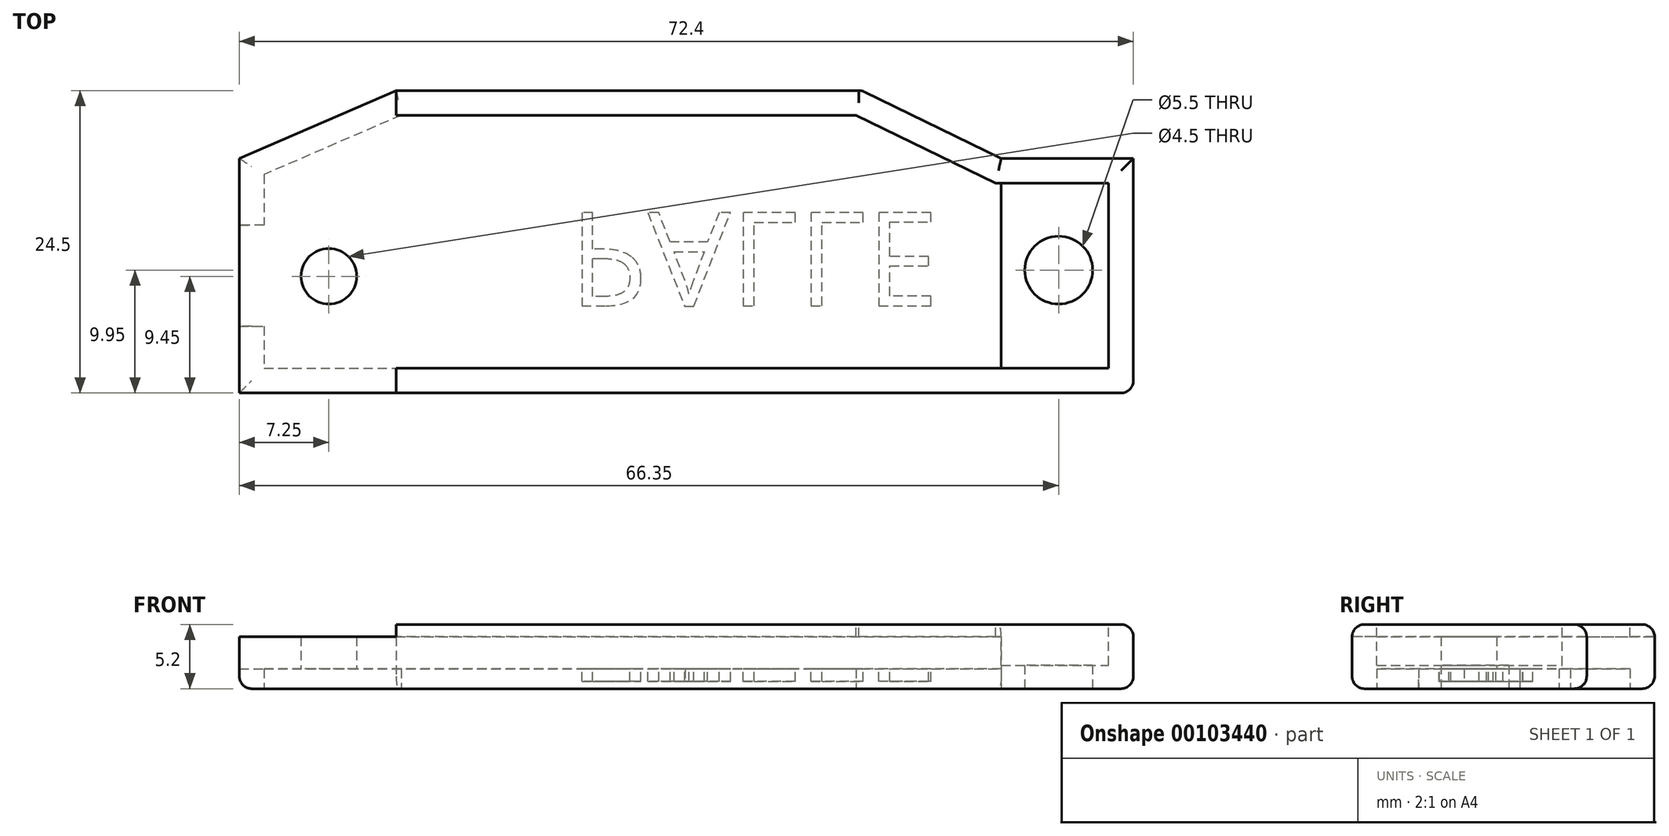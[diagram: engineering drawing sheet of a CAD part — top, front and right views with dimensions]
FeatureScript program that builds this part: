
annotation { "Feature Type Name" : "Feature", "Feature Type Description" : "" }
export const myFeature = defineFeature(function(context is Context, id is Id, definition is map)
    precondition{}
    {
        {
            var Q0;
            Q0=qCreatedBy(makeId("Top.planeOp"),FACE);
            var sketch = newSketch(context, id + "F0", { "sketchPlane" : qUnion([Q0])});
            skLineSegment(sketch, "E0.bottom", {"start": v(-23.5, 12.25) * mm, "end": v(14.2, 12.25) * mm});
            skLineSegment(sketch, "E0.top", {"start": v(-36.2, -12.25) * mm, "end": v(36.2, -12.25) * mm});
            skLineSegment(sketch, "E0.left", {"start": v(-36.2, 6.75) * mm, "end": v(-36.2, -12.25) * mm});
            skLineSegment(sketch, "E0.right", {"start": v(36.2, 6.75) * mm, "end": v(36.2, -12.25) * mm});
            skCircle(sketch, "E1", {"center": v(-28.95, -2.8) * mm, "radius": 2.25 * mm});
            skCircle(sketch, "E2", {"center": v(30.15, -2.3) * mm, "radius": 2.75 * mm});
            skLineSegment(sketch, "E3", {"start": v(36.2, 6.75) * mm, "end": v(25.5, 6.75) * mm});
            skLineSegment(sketch, "E4", {"start": v(25.5, 6.75) * mm, "end": v(14.2, 12.25) * mm});
            skLineSegment(sketch, "E5", {"start": v(-36.2, 6.75) * mm, "end": v(-23.5, 12.25) * mm});
            skPoint(sketch, "E6.orphan", {"position": v(-36.2, 12.25) * mm});
            skPoint(sketch, "E7.orphan", {"position": v(36.2, 12.25) * mm});
            skSolve(sketch);
        }
        {
            var Q0;
            Q0 = qSketchRegion(id + "F0", true);
            extrude(context, id + "F1", {"entities" : qUnion([Q0]), "depth" : 5.2 * mm});
        }
        {
            var Q0;
            Q0=makeQuery(id+"F1.opExtrude","CAP_FACE",FACE,{"disambiguationData":[OSD([sQuery(id+"F0.wireOp",EDGE,"E0.bottom"),sQuery(id+"F0.wireOp",EDGE,"E0.top"),sQuery(id+"F0.wireOp",EDGE,"E0.left"),sQuery(id+"F0.wireOp",EDGE,"E0.right"),sQuery(id+"F0.wireOp",EDGE,"E1"),sQuery(id+"F0.wireOp",EDGE,"E2"),sQuery(id+"F0.wireOp",EDGE,"E3"),sQuery(id+"F0.wireOp",EDGE,"E4"),sQuery(id+"F0.wireOp",EDGE,"E5")])],"isStart":true});
            var sketch = newSketch(context, id + "F2", { "sketchPlane" : qUnion([Q0])});
            skLineSegment(sketch, "E8", {"start": v(-36.2, 6.85) * mm, "end": v(-34.2, 6.85) * mm});
            skLineSegment(sketch, "E9", {"start": v(-34.2, 6.85) * mm, "end": v(-34.2, 10.25) * mm});
            skLineSegment(sketch, "E10", {"start": v(-34.2, 10.25) * mm, "end": v(25.5, 10.25) * mm});
            skLineSegment(sketch, "E11", {"start": v(25.5, 10.25) * mm, "end": v(25.5, -4.53) * mm});
            skLineSegment(sketch, "E12", {"start": v(25.5, -4.53) * mm, "end": v(13.74, -10.25) * mm});
            skLineSegment(sketch, "E13", {"start": v(13.74, -10.25) * mm, "end": v(-23.09, -10.25) * mm});
            skLineSegment(sketch, "E14", {"start": v(-23.09, -10.25) * mm, "end": v(-34.2, -5.44) * mm});
            skLineSegment(sketch, "E15", {"start": v(-34.2, -5.44) * mm, "end": v(-34.2, -1.35) * mm});
            skLineSegment(sketch, "E16", {"start": v(-34.2, -1.35) * mm, "end": v(-36.2, -1.35) * mm});
            skLineSegment(sketch, "E17", {"start": v(-36.2, -1.35) * mm, "end": v(-36.2, 6.85) * mm});
            skLineSegment(sketch, "E18", {"start": v(25.5, -6.75) * mm, "end": v(25.5, 23.06) * mm, "construction": true});
            skSolve(sketch);
        }
        {
            var Q0;
            Q0=makeQuery(id+"F2.imprint","IMPRINT",FACE,{"disambiguationData":[TD([[makeQuery(id+"F2.imprint","IMPRINT",EDGE,{"derivedFrom":sQuery(id+"F2.wireOp",EDGE,"E8")}),-1.0]])]});
            extrude(context, id + "F3", {"entities" : qUnion([Q0]), "operationType" : NewBodyOperationType.REMOVE, "oppositeDirection" : true, "depth" : 1.6 * mm});
        }
        {
            var Q0;
            Q0=makeQuery(id+"F1.opExtrude","CAP_FACE",FACE,{"disambiguationData":[OSD([sQuery(id+"F0.wireOp",EDGE,"E0.bottom"),sQuery(id+"F0.wireOp",EDGE,"E0.top"),sQuery(id+"F0.wireOp",EDGE,"E0.left"),sQuery(id+"F0.wireOp",EDGE,"E0.right"),sQuery(id+"F0.wireOp",EDGE,"E1"),sQuery(id+"F0.wireOp",EDGE,"E2"),sQuery(id+"F0.wireOp",EDGE,"E3"),sQuery(id+"F0.wireOp",EDGE,"E4"),sQuery(id+"F0.wireOp",EDGE,"E5")])],"isStart":false});
            var sketch = newSketch(context, id + "F4", { "sketchPlane" : qUnion([Q0])});
            skLineSegment(sketch, "E19", {"start": v(-36.2, -12.25) * mm, "end": v(-36.2, 6.75) * mm});
            skLineSegment(sketch, "E20", {"start": v(-23.5, 12.25) * mm, "end": v(-23.5, 10.25) * mm});
            skLineSegment(sketch, "E21", {"start": v(-23.5, -12.25) * mm, "end": v(-36.2, -12.25) * mm});
            skLineSegment(sketch, "E22", {"start": v(-36.2, 6.75) * mm, "end": v(-23.5, 12.25) * mm});
            skLineSegment(sketch, "E23", {"start": v(25.5, 6.75) * mm, "end": v(25.5, -38.98) * mm, "construction": true});
            skLineSegment(sketch, "E24", {"start": v(-23.5, -10.25) * mm, "end": v(25.5, -10.25) * mm});
            skLineSegment(sketch, "E25", {"start": v(25.5, -10.25) * mm, "end": v(25.5, 4.53) * mm});
            skLineSegment(sketch, "E26", {"start": v(25.5, 4.53) * mm, "end": v(13.74, 10.25) * mm});
            skLineSegment(sketch, "E27", {"start": v(13.74, 10.25) * mm, "end": v(-23.5, 10.25) * mm});
            skLineSegment(sketch, "E28.trimOffspring", {"start": v(-23.5, -10.25) * mm, "end": v(-23.5, -12.25) * mm});
            skSolve(sketch);
        }
        {
            var Q0;
            Q0 = qSketchRegion(id + "F4", true);
            extrude(context, id + "F5", {"entities" : qUnion([Q0]), "operationType" : NewBodyOperationType.REMOVE, "oppositeDirection" : true, "depth" : 1 * mm});
        }
        {
            var Q0;
            Q0=makeQuery(id+"F1.opExtrude","CAP_FACE",FACE,{"disambiguationData":[OSD([sQuery(id+"F0.wireOp",EDGE,"E0.bottom"),sQuery(id+"F0.wireOp",EDGE,"E0.top"),sQuery(id+"F0.wireOp",EDGE,"E0.left"),sQuery(id+"F0.wireOp",EDGE,"E0.right"),sQuery(id+"F0.wireOp",EDGE,"E1"),sQuery(id+"F0.wireOp",EDGE,"E2"),sQuery(id+"F0.wireOp",EDGE,"E3"),sQuery(id+"F0.wireOp",EDGE,"E4"),sQuery(id+"F0.wireOp",EDGE,"E5")])],"isStart":false});
            var sketch = newSketch(context, id + "F6", { "sketchPlane" : qUnion([Q0])});
            skLineSegment(sketch, "E29.bottom", {"start": v(25.5, -10.25) * mm, "end": v(34.2, -10.25) * mm});
            skLineSegment(sketch, "E29.top", {"start": v(25.5, 4.75) * mm, "end": v(34.2, 4.75) * mm});
            skLineSegment(sketch, "E29.left", {"start": v(25.5, -10.25) * mm, "end": v(25.5, 4.75) * mm});
            skLineSegment(sketch, "E29.right", {"start": v(34.2, -10.25) * mm, "end": v(34.2, 4.75) * mm});
            skSolve(sketch);
        }
        {
            var Q0;
            Q0 = qSketchRegion(id + "F6", true);
            extrude(context, id + "F7", {"entities" : qUnion([Q0]), "operationType" : NewBodyOperationType.REMOVE, "oppositeDirection" : true, "depth" : 3.3 * mm});
        }
        {
            var Q0;
            Q0=makeQuery(id+"F7.boolean.opBoolean","MERGE",EDGE,{"derivedFrom":[makeQuery(id+"F5.boolean.opBoolean","COPY",EDGE,{"derivedFrom":makeQuery(id+"F5.opExtrude","CAP_EDGE",EDGE,{"disambiguationData":[OSD([sQuery(id+"F4.wireOp",EDGE,"E24")])],"isStart":true})}),makeQuery(id+"F7.opExtrude","CAP_EDGE",EDGE,{"disambiguationData":[OSD([sQuery(id+"F6.wireOp",EDGE,"E29.bottom")])],"isStart":true})]});
            var Q1;
            Q1=makeQuery(id+"F1.opExtrude","CAP_EDGE",EDGE,{"disambiguationData":[OSD([sQuery(id+"F0.wireOp",EDGE,"E0.top")])],"isStart":false});
            var Q2;
            Q2=makeQuery(id+"F5.boolean.opBoolean","COPY",EDGE,{"derivedFrom":makeQuery(id+"F5.opExtrude","CAP_EDGE",EDGE,{"disambiguationData":[OSD([sQuery(id+"F4.wireOp",EDGE,"E27")])],"isStart":true})});
            var Q3;
            Q3=makeQuery(id+"F1.opExtrude","CAP_EDGE",EDGE,{"disambiguationData":[OSD([sQuery(id+"F0.wireOp",EDGE,"E0.bottom")])],"isStart":false});
            fillet(context, id + "F8", {"entities" : qUnion([Q0, Q1, Q2, Q3]), "radius" : 1 * mm, "tangentPropagation" : true, "allowEdgeOverflow" : false});
        }
        {
            var Q0;
            Q0=makeQuery(id+"F1.opExtrude","CAP_FACE",FACE,{"disambiguationData":[OSD([sQuery(id+"F0.wireOp",EDGE,"E0.bottom"),sQuery(id+"F0.wireOp",EDGE,"E0.top"),sQuery(id+"F0.wireOp",EDGE,"E0.left"),sQuery(id+"F0.wireOp",EDGE,"E0.right"),sQuery(id+"F0.wireOp",EDGE,"E1"),sQuery(id+"F0.wireOp",EDGE,"E2"),sQuery(id+"F0.wireOp",EDGE,"E3"),sQuery(id+"F0.wireOp",EDGE,"E4"),sQuery(id+"F0.wireOp",EDGE,"E5")])],"isStart":false});
            var sketch = newSketch(context, id + "F9", { "sketchPlane" : qUnion([Q0])});
            skLineSegment(sketch, "E30", {"start": v(25.5, 4.75) * mm, "end": v(24.86, 4.75) * mm});
            skLineSegment(sketch, "E31", {"start": v(24.86, 4.75) * mm, "end": v(25.5, 4.53) * mm});
            skLineSegment(sketch, "E32", {"start": v(25.5, 4.53) * mm, "end": v(25.5, 4.75) * mm});
            skSolve(sketch);
        }
        {
            var Q0;
            Q0 = qSketchRegion(id + "F9", true);
            extrude(context, id + "F10", {"entities" : qUnion([Q0]), "operationType" : NewBodyOperationType.REMOVE, "oppositeDirection" : true, "depth" : 1 * mm});
        }
        {
            var Q0;
            Q0=makeQuery(id+"F5.boolean.opBoolean","COPY",EDGE,{"derivedFrom":makeQuery(id+"F5.opExtrude","CAP_EDGE",EDGE,{"disambiguationData":[OSD([sQuery(id+"F4.wireOp",EDGE,"E26")])],"isStart":true})});
            var Q1;
            Q1=makeQuery(id+"F1.opExtrude","CAP_EDGE",EDGE,{"disambiguationData":[OSD([sQuery(id+"F0.wireOp",EDGE,"E4")])],"isStart":false});
            var Q2;
            Q2=makeQuery(id+"F1.opExtrude","CAP_EDGE",EDGE,{"disambiguationData":[OSD([sQuery(id+"F0.wireOp",EDGE,"E3")])],"isStart":false});
            var Q3;
            Q3=makeQuery(id+"F10.boolean.opBoolean","MERGE",EDGE,{"derivedFrom":[makeQuery(id+"F7.boolean.opBoolean","COPY",EDGE,{"derivedFrom":makeQuery(id+"F7.opExtrude","CAP_EDGE",EDGE,{"disambiguationData":[OSD([sQuery(id+"F6.wireOp",EDGE,"E29.top")])],"isStart":true})}),makeQuery(id+"F10.opExtrude","CAP_EDGE",EDGE,{"disambiguationData":[OSD([sQuery(id+"F9.wireOp",EDGE,"E30")])],"isStart":true})]});
            var Q4;
            Q4=makeQuery(id+"F7.boolean.opBoolean","COPY",EDGE,{"derivedFrom":makeQuery(id+"F7.opExtrude","CAP_EDGE",EDGE,{"disambiguationData":[OSD([sQuery(id+"F6.wireOp",EDGE,"E29.right")])],"isStart":true})});
            var Q5;
            Q5=makeQuery(id+"F1.opExtrude","CAP_EDGE",EDGE,{"disambiguationData":[OSD([sQuery(id+"F0.wireOp",EDGE,"E0.right")])],"isStart":false});
            fillet(context, id + "F11", {"entities" : qUnion([Q0, Q1, Q2, Q3, Q4, Q5]), "radius" : 1 * mm, "tangentPropagation" : true, "allowEdgeOverflow" : false});
        }
        {
            var Q0;
            Q0=makeQuery(id+"F5.boolean.opBoolean","COPY",EDGE,{"derivedFrom":makeQuery(id+"F5.opExtrude","CAP_EDGE",EDGE,{"disambiguationData":[OSD([sQuery(id+"F4.wireOp",EDGE,"E21")])],"isStart":false})});
            var Q1;
            Q1=makeQuery(id+"F5.boolean.opBoolean","COPY",EDGE,{"derivedFrom":makeQuery(id+"F5.opExtrude","CAP_EDGE",EDGE,{"disambiguationData":[OSD([sQuery(id+"F4.wireOp",EDGE,"E19")])],"isStart":false})});
            var Q2;
            Q2=makeQuery(id+"F5.boolean.opBoolean","COPY",EDGE,{"derivedFrom":makeQuery(id+"F5.opExtrude","CAP_EDGE",EDGE,{"disambiguationData":[OSD([sQuery(id+"F4.wireOp",EDGE,"E22")])],"isStart":false})});
            var Q3;
            Q3=makeQuery(id+"F10.boolean.opBoolean","MERGE",EDGE,{"derivedFrom":[makeQuery(id+"F5.boolean.opBoolean","COPY",EDGE,{"derivedFrom":makeQuery(id+"F5.opExtrude","CAP_EDGE",EDGE,{"disambiguationData":[OSD([sQuery(id+"F4.wireOp",EDGE,"E25")])],"isStart":false})}),makeQuery(id+"F10.opExtrude","CAP_EDGE",EDGE,{"disambiguationData":[OSD([sQuery(id+"F9.wireOp",EDGE,"E32")])],"isStart":false})]});
            var Q4;
            Q4=makeQuery(id+"F1.opExtrude","CAP_EDGE",EDGE,{"disambiguationData":[OSD([sQuery(id+"F0.wireOp",EDGE,"E3")])],"isStart":true});
            var Q5;
            Q5=makeQuery(id+"F1.opExtrude","CAP_EDGE",EDGE,{"disambiguationData":[OSD([sQuery(id+"F0.wireOp",EDGE,"E0.right")])],"isStart":true});
            var Q6;
            Q6=makeQuery(id+"F1.opExtrude","CAP_EDGE",EDGE,{"disambiguationData":[OSD([sQuery(id+"F0.wireOp",EDGE,"E4")])],"isStart":true});
            var Q7;
            Q7=makeQuery(id+"F1.opExtrude","CAP_EDGE",EDGE,{"disambiguationData":[OSD([sQuery(id+"F0.wireOp",EDGE,"E5")])],"isStart":true});
            var Q8;
            Q8=makeQuery(id+"F3.boolean.opBoolean","COPY",EDGE,{"derivedFrom":makeQuery(id+"F3.opExtrude","CAP_EDGE",EDGE,{"disambiguationData":[OSD([sQuery(id+"F2.wireOp",EDGE,"E12")])],"isStart":true})});
            var Q9;
            Q9=makeQuery(id+"F3.boolean.opBoolean","COPY",EDGE,{"derivedFrom":makeQuery(id+"F3.opExtrude","CAP_EDGE",EDGE,{"disambiguationData":[OSD([sQuery(id+"F2.wireOp",EDGE,"E13")])],"isStart":true})});
            var Q10;
            Q10=makeQuery(id+"F3.boolean.opBoolean","COPY",EDGE,{"derivedFrom":makeQuery(id+"F3.opExtrude","CAP_EDGE",EDGE,{"disambiguationData":[OSD([sQuery(id+"F2.wireOp",EDGE,"E14")])],"isStart":true})});
            var Q11;
            Q11=makeQuery(id+"F3.boolean.opBoolean","COPY",EDGE,{"derivedFrom":makeQuery(id+"F3.opExtrude","CAP_EDGE",EDGE,{"disambiguationData":[OSD([sQuery(id+"F2.wireOp",EDGE,"E17")])],"isStart":false})});
            var Q12;
            {var subQ0=sQuery(id+"F0.wireOp",EDGE,"E5");var subQ1=sQuery(id+"F0.wireOp",EDGE,"E0.left");Q12=makeQuery(id+"F3.boolean.opBoolean","SPLIT",EDGE,{"disambiguationData":[TD([makeQuery(id+"F1.opExtrude","SWEPT_FACE",FACE,{"disambiguationData":[OSD([subQ0])]})])],"derivedFrom":makeQuery(id+"F1.opExtrude","CAP_EDGE",EDGE,{"disambiguationData":[OSD([subQ1])],"isStart":true})});}
            var Q13;
            Q13=makeQuery(id+"F3.boolean.opBoolean","COPY",EDGE,{"derivedFrom":makeQuery(id+"F3.opExtrude","CAP_EDGE",EDGE,{"disambiguationData":[OSD([sQuery(id+"F2.wireOp",EDGE,"E15")])],"isStart":true})});
            var Q14;
            Q14=makeQuery(id+"F3.boolean.opBoolean","COPY",EDGE,{"derivedFrom":makeQuery(id+"F3.opExtrude","CAP_EDGE",EDGE,{"disambiguationData":[OSD([sQuery(id+"F2.wireOp",EDGE,"E9")])],"isStart":true})});
            var Q15;
            {var subQ0=sQuery(id+"F0.wireOp",EDGE,"E0.left");var subQ1=sQuery(id+"F0.wireOp",EDGE,"E0.top");Q15=makeQuery(id+"F3.boolean.opBoolean","SPLIT",EDGE,{"disambiguationData":[TD([makeQuery(id+"F1.opExtrude","SWEPT_FACE",FACE,{"disambiguationData":[OSD([subQ1])]})])],"derivedFrom":makeQuery(id+"F1.opExtrude","CAP_EDGE",EDGE,{"disambiguationData":[OSD([subQ0])],"isStart":true})});}
            var Q16;
            Q16=makeQuery(id+"F3.boolean.opBoolean","COPY",EDGE,{"derivedFrom":makeQuery(id+"F3.opExtrude","CAP_EDGE",EDGE,{"disambiguationData":[OSD([sQuery(id+"F2.wireOp",EDGE,"E10")])],"isStart":true})});
            var Q17;
            Q17=makeQuery(id+"F3.boolean.opBoolean","COPY",EDGE,{"derivedFrom":makeQuery(id+"F3.opExtrude","CAP_EDGE",EDGE,{"disambiguationData":[OSD([sQuery(id+"F2.wireOp",EDGE,"E11")])],"isStart":true})});
            fillet(context, id + "F12", {"entities" : qUnion([Q0, Q1, Q2, Q3, Q4, Q5, Q6, Q7, Q8, Q9, Q10, Q11, Q12, Q13, Q14, Q15, Q16, Q17]), "radius" : 1 * mm, "tangentPropagation" : true, "allowEdgeOverflow" : false});
        }
        {
            var Q0;
            Q0=makeQuery(id+"F3.boolean.opBoolean","COPY",FACE,{"derivedFrom":makeQuery(id+"F3.opExtrude","CAP_FACE",FACE,{"disambiguationData":[OSD([sQuery(id+"F0.wireOp",EDGE,"E1"),sQuery(id+"F2.wireOp",EDGE,"E8"),sQuery(id+"F2.wireOp",EDGE,"E9"),sQuery(id+"F2.wireOp",EDGE,"E10"),sQuery(id+"F2.wireOp",EDGE,"E11"),sQuery(id+"F2.wireOp",EDGE,"E12"),sQuery(id+"F2.wireOp",EDGE,"E13"),sQuery(id+"F2.wireOp",EDGE,"E14"),sQuery(id+"F2.wireOp",EDGE,"E15"),sQuery(id+"F2.wireOp",EDGE,"E16"),sQuery(id+"F2.wireOp",EDGE,"E17")])],"isStart":false})});
            var sketch = newSketch(context, id + "F13", { "sketchPlane" : qUnion([Q0])});
            skText(sketch, "E33", { "text": "PALLE", "fontName": "OpenSans-Regular.ttf"});
            const initialGuessF13  = {"E33": [-0.0095, -0.00237, 1, 0, 0.00762]};
            skSetInitialGuess(sketch, initialGuessF13);
            skSolve(sketch);
        }
        {
            var Q0;
            Q0 = qSketchRegion(id + "F13", true);
            extrude(context, id + "F14", {"entities" : qUnion([Q0]), "operationType" : NewBodyOperationType.ADD, "depth" : 1 * mm});
        }
    });
